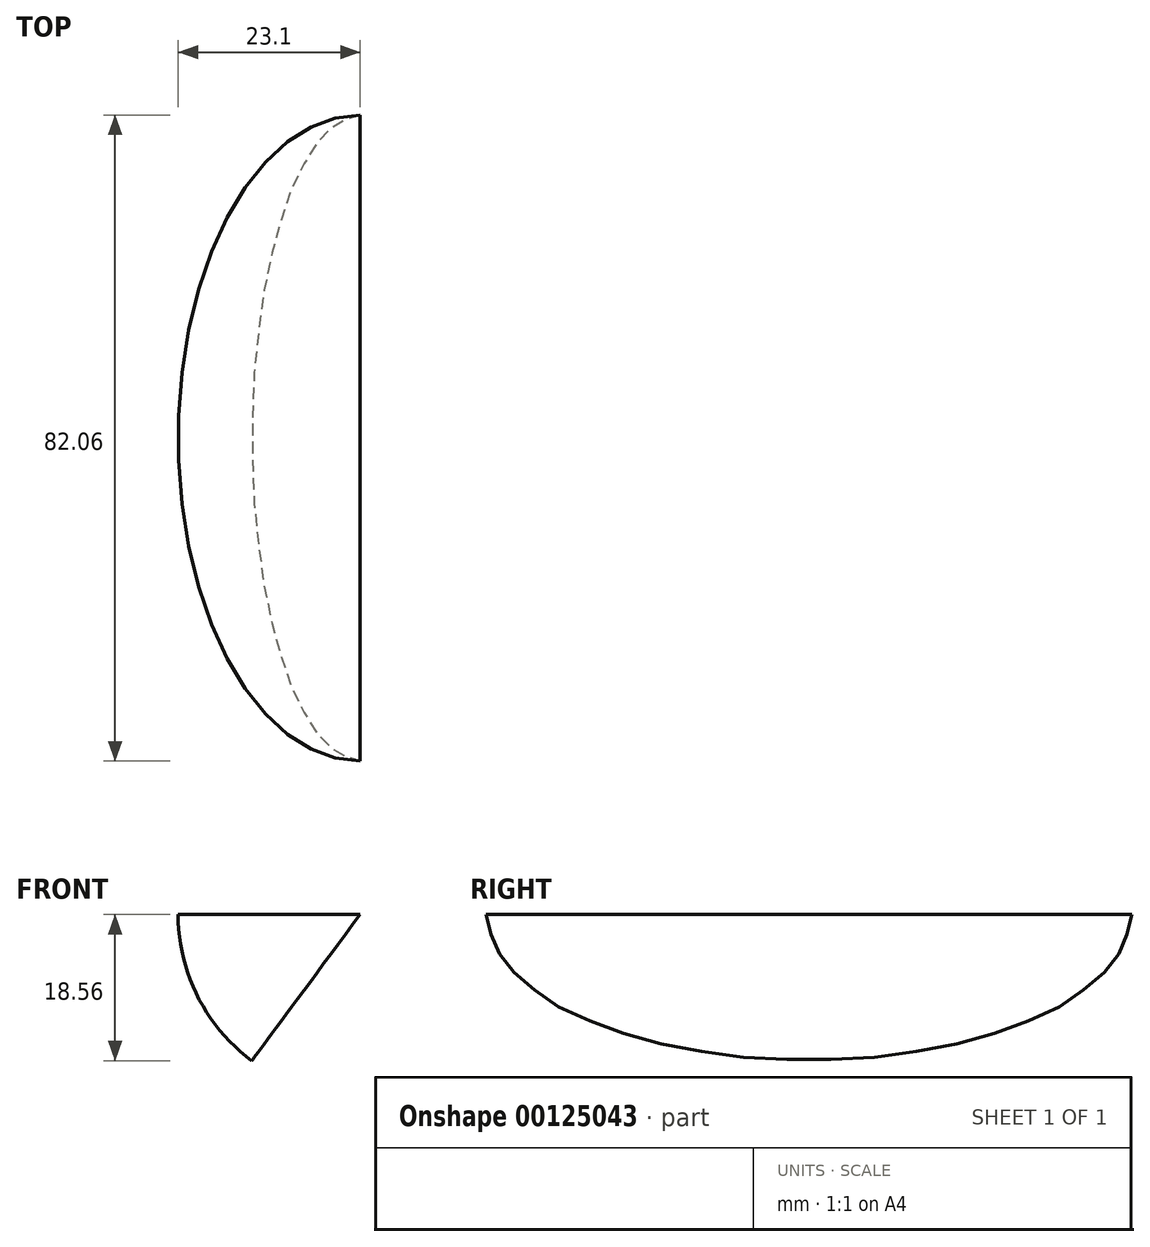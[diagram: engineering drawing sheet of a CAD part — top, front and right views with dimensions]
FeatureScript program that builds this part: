
annotation { "Feature Type Name" : "Feature", "Feature Type Description" : "" }
export const myFeature = defineFeature(function(context is Context, id is Id, definition is map)
    precondition{}
    {
        {
            var Q0;
            Q0=qCreatedBy(makeId("Top.planeOp"),FACE);
            var sketch = newSketch(context, id + "F0", { "sketchPlane" : qUnion([Q0])});
            skEllipticalArc(sketch, "E0", {});
            skLineSegment(sketch, "E1", {"start": v(0, 41.03) * mm, "end": v(0, -41.03) * mm});
            const initialGuessF0  = {"E0": [0, 0, 0, 1, 0.041028439786135976, 0.0231015269360061, 0, 3.141592653589793]};
            skSetInitialGuess(sketch, initialGuessF0);
            skSolve(sketch);
        }
        {
            var Q0;
            Q0=makeQuery(id+"F0.imprint","IMPRINT",FACE,{"disambiguationData":[TD([[makeQuery(id+"F0.imprint","IMPRINT",EDGE,{"derivedFrom":sQuery(id+"F0.wireOp",EDGE,"E0")}),1.0]])]});
            var Q1;
            Q1=sQuery(id+"F0.wireOp",EDGE,"E1");
            revolve(context, id + "F1", {"entities" : qUnion([Q0]), "axis" : qUnion([Q1]), "revolveType" : RevolveType.ONE_DIRECTION, "angle" : 53.47 * degree});
        }
    });
